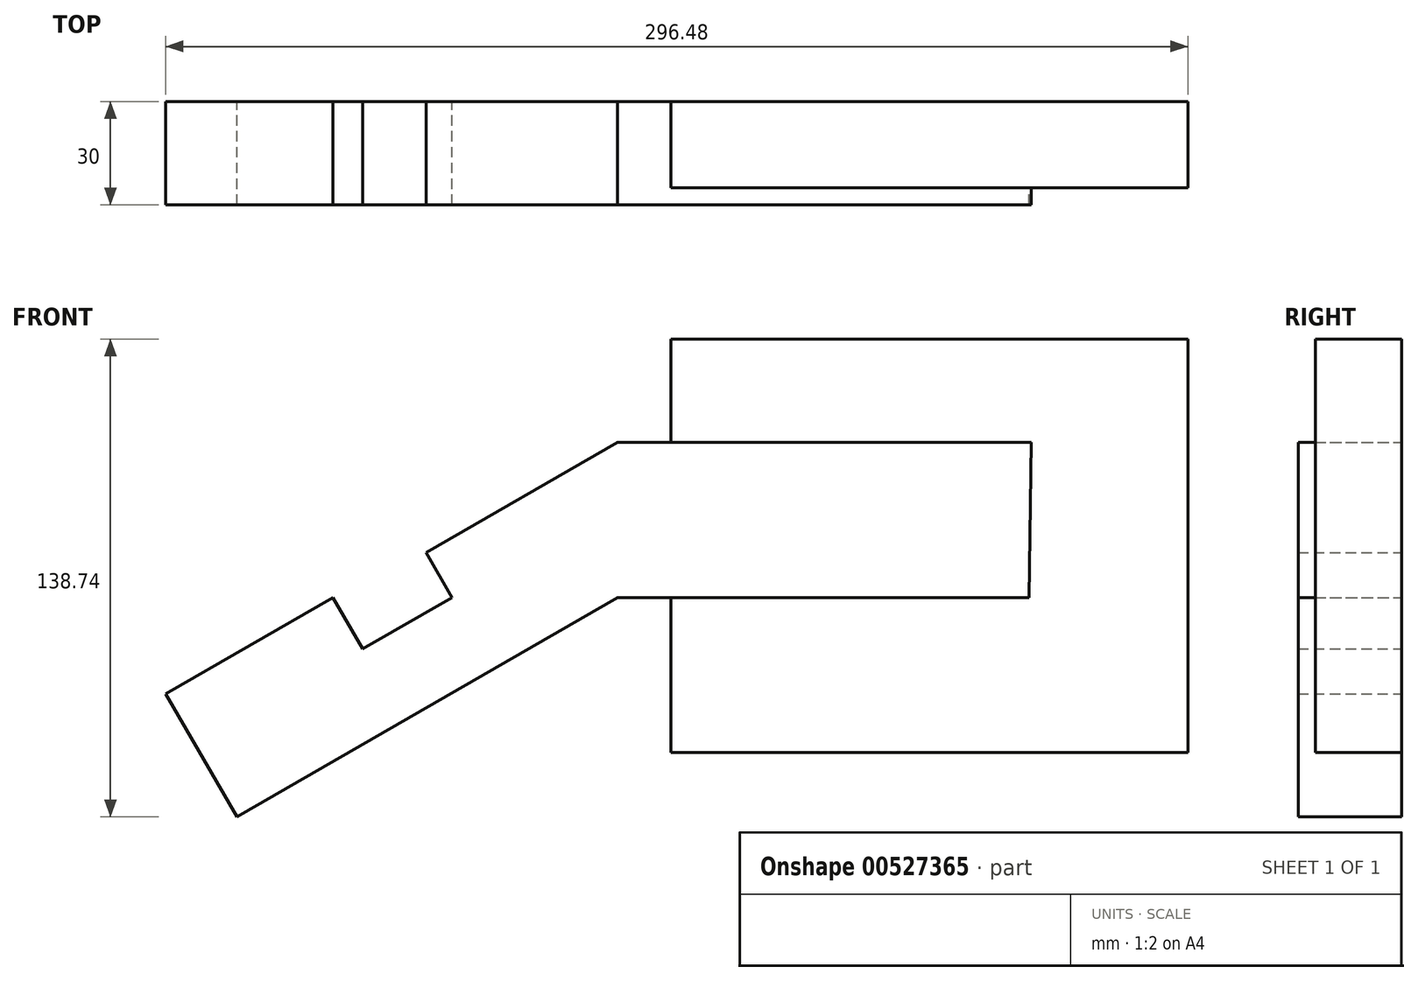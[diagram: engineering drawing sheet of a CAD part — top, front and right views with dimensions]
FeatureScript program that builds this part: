
annotation { "Feature Type Name" : "Feature", "Feature Type Description" : "" }
export const myFeature = defineFeature(function(context is Context, id is Id, definition is map)
    precondition{}
    {
        {
            var Q0;
            Q0=qCreatedBy(makeId("Front.planeOp"),FACE);
            var sketch = newSketch(context, id + "F0", { "sketchPlane" : qUnion([Q0])});
            skLineSegment(sketch, "E0", {"start": v(65.5, 0) * mm, "end": v(-53.85, 0) * mm});
            skLineSegment(sketch, "E1", {"start": v(-53.85, 0) * mm, "end": v(-164.26, -63.74) * mm});
            skLineSegment(sketch, "E2", {"start": v(-164.26, -63.74) * mm, "end": v(-184.88, -28.03) * mm});
            skLineSegment(sketch, "E3", {"start": v(-184.88, -28.03) * mm, "end": v(-136.33, 0) * mm});
            skLineSegment(sketch, "E4", {"start": v(-136.33, 0) * mm, "end": v(-127.7, -14.96) * mm});
            skLineSegment(sketch, "E5", {"start": v(-127.7, -14.96) * mm, "end": v(-101.79, 0) * mm});
            skLineSegment(sketch, "E6", {"start": v(-101.79, 0) * mm, "end": v(-109.29, 13) * mm});
            skLineSegment(sketch, "E7", {"start": v(-109.29, 13) * mm, "end": v(-53.85, 45) * mm});
            skLineSegment(sketch, "E8", {"start": v(-53.85, 45) * mm, "end": v(66.15, 45) * mm});
            skLineSegment(sketch, "E9", {"start": v(66.15, 45) * mm, "end": v(65.5, 0) * mm});
            skLineSegment(sketch, "E10", {"start": v(-38.4, 45) * mm, "end": v(-38.4, 75) * mm});
            skLineSegment(sketch, "E11", {"start": v(-38.4, 75) * mm, "end": v(111.6, 75) * mm});
            skLineSegment(sketch, "E12", {"start": v(111.6, 75) * mm, "end": v(111.6, -45) * mm});
            skLineSegment(sketch, "E13", {"start": v(111.6, -45) * mm, "end": v(-38.4, -45) * mm});
            skLineSegment(sketch, "E14", {"start": v(-38.4, -45) * mm, "end": v(-38.4, 0) * mm});
            skSolve(sketch);
        }
        {
            var Q0;
            {var subQ6=sQuery(id+"F0.wireOp",EDGE,"E1");Q0=makeQuery(id+"F0.imprint","IMPRINT",FACE,{"disambiguationData":[TD([[makeQuery(id+"F0.imprint","IMPRINT",EDGE,{"derivedFrom":subQ6}),-1.0]])]});}
            extrude(context, id + "F1", {"entities" : qUnion([Q0]), "depth" : 30 * mm, "offsetDistance" : 25 * mm});
        }
        {
            var Q0;
            Q0 = qSketchRegion(id + "F0", true);
            extrude(context, id + "F2", {"entities" : qUnion([Q0]), "operationType" : NewBodyOperationType.ADD, "depth" : 25 * mm, "offsetDistance" : 25 * mm});
        }
    });
